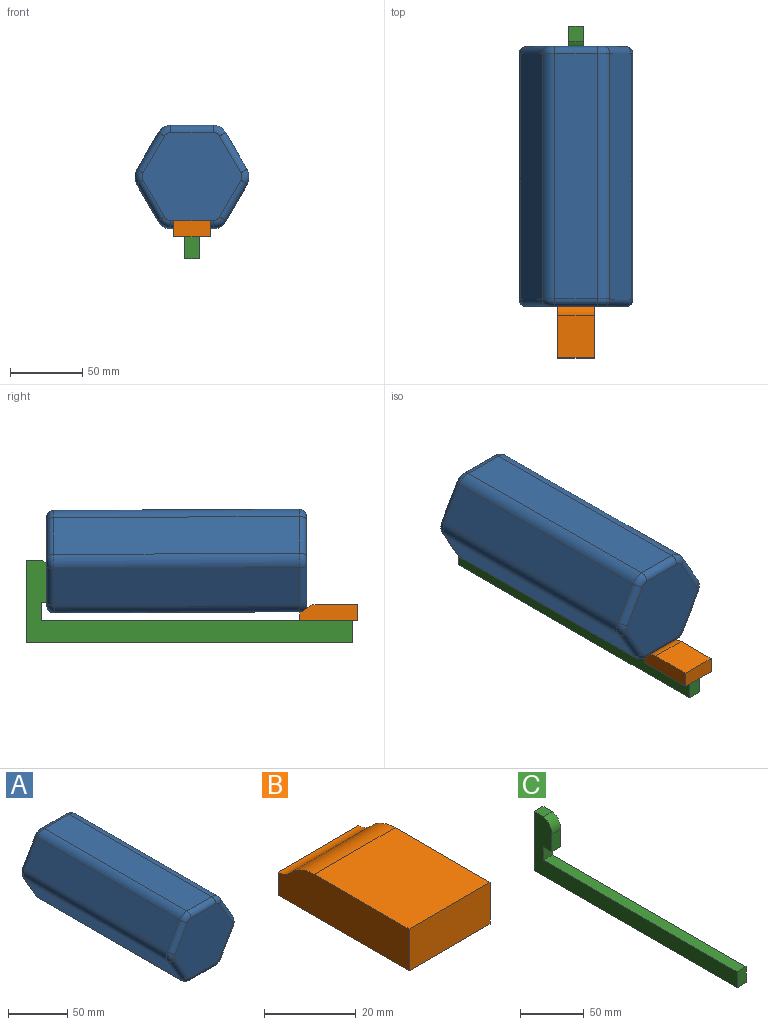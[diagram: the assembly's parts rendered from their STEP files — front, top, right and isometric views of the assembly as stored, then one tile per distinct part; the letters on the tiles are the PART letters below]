
ASSEMBLY  parts=3 mates=2
PART A: 47 faces, bbox 80.6x180x72.7 mm
  f0: plane 68.91x61.01mm, normal (0,1,0), area 2910.8mm2, adj f1,f15,f16,f17,f18,f19,f20,f21
  f1: cylinder r=5mm len=9.73mm, axis (1,0,0), area 76.4mm2, adj f0,f12,f17,f42
  f2: plane 170x25.51mm, normal (0.87,0,-0.5), area 5007mm2, adj f3,f13,f19,f31
  f3: cylinder r=10mm len=170mm, axis (0,1,0), area 1780.2mm2, adj f2,f4,f21,f33
  f4: plane 170x25.51mm, normal (0.87,0,0.5), area 5007mm2, adj f3,f5,f23,f35
  f5: cylinder r=10mm len=170mm, axis (0,1,0), area 1780.2mm2, adj f4,f6,f25,f37
  f6: plane 170x29.45mm, normal (0,0,1), area 5007mm2, adj f5,f7,f26,f38
  f7: cylinder r=10mm len=170mm, axis (0,1,0), area 1780.2mm2, adj f6,f8,f24,f36
  f8: plane 170x25.51mm, normal (-0.87,0,0.5), area 5007mm2, adj f7,f9,f22,f34
  f9: cylinder r=10mm len=170mm, axis (0,1,0), area 1780.2mm2, adj f8,f10,f20,f32
  f10: plane 170x25.51mm, normal (-0.87,0,-0.5), area 5007mm2, adj f9,f11,f18,f30
  f11: cylinder r=10mm len=170mm, axis (0,1,0), area 1780.2mm2, adj f10,f12,f16,f28
  f12: plane 170x29.45mm, normal (0,0,-1), area 5007mm2, adj f1,f11,f13,f15,f27,f44
  f13: cylinder r=10mm len=170mm, axis (0,1,0), area 1780.2mm2, adj f2,f12,f17,f29
  f14: plane 68.91x61.01mm, normal (0,-1,0), area 3215.9mm2, adj f27,f28,f29,f30,f31,f32,f33,f34
  f15: cylinder r=5mm len=9.73mm, axis (1,0,0), area 76.4mm2, adj f0,f12,f16,f43
  f16: torus R=5mm, axis (0,-1,0), area 67.3mm2, adj f0,f11,f15,f18
  f17: torus R=5mm, axis (0,-1,0), area 67.3mm2, adj f0,f1,f13,f19
  f18: cylinder r=5mm len=28.01mm, axis (0.5,0,-0.87), area 231.3mm2, adj f0,f10,f16,f20
  f19: cylinder r=5mm len=28.01mm, axis (0.5,0,0.87), area 231.3mm2, adj f0,f2,f17,f21
  f20: torus R=5mm, axis (0,-1,0), area 67.3mm2, adj f0,f9,f18,f22
  f21: torus R=5mm, axis (0,-1,0), area 67.3mm2, adj f0,f3,f19,f23
  f22: cylinder r=5mm len=28.01mm, axis (-0.5,0,-0.87), area 231.3mm2, adj f0,f8,f20,f24
  f23: cylinder r=5mm len=28.01mm, axis (-0.5,0,0.87), area 231.3mm2, adj f0,f4,f21,f25
  f24: torus R=5mm, axis (0,-1,0), area 67.3mm2, adj f0,f7,f22,f26
  f25: torus R=5mm, axis (0,-1,0), area 67.3mm2, adj f0,f5,f23,f26
  f26: cylinder r=5mm len=29.45mm, axis (-1,0,0), area 231.3mm2, adj f0,f6,f24,f25
  f27: cylinder r=5mm len=29.45mm, axis (-1,0,0), area 231.3mm2, adj f12,f14,f28,f29
  f28: torus R=5mm, axis (0,-1,0), area 67.3mm2, adj f11,f14,f27,f30
  f29: torus R=5mm, axis (0,-1,0), area 67.3mm2, adj f13,f14,f27,f31
  f30: cylinder r=5mm len=28.01mm, axis (-0.5,0,0.87), area 231.3mm2, adj f10,f14,f28,f32
  f31: cylinder r=5mm len=28.01mm, axis (-0.5,0,-0.87), area 231.3mm2, adj f2,f14,f29,f33
  f32: torus R=5mm, axis (0,-1,0), area 67.3mm2, adj f9,f14,f30,f34
  f33: torus R=5mm, axis (0,-1,0), area 67.3mm2, adj f3,f14,f31,f35
  f34: cylinder r=5mm len=28.01mm, axis (0.5,0,0.87), area 231.3mm2, adj f8,f14,f32,f36
  f35: cylinder r=5mm len=28.01mm, axis (0.5,0,-0.87), area 231.3mm2, adj f4,f14,f33,f37
  f36: torus R=5mm, axis (0,-1,0), area 67.3mm2, adj f7,f14,f34,f38
  f37: torus R=5mm, axis (0,-1,0), area 67.3mm2, adj f5,f14,f35,f38
  f38: cylinder r=5mm len=29.45mm, axis (1,0,0), area 231.3mm2, adj f6,f14,f36,f37
  f39: cylinder r=12.48mm len=12.09mm, axis (-1,0,0), area 164.6mm2, adj f0,f40,f42,f43
  f40: plane 16.95x10mm, normal (0,1,0), area 169.5mm2, adj f39,f41,f42,f43
  f41: plane 10x8.36mm, normal (0,0,1), area 83.6mm2, adj f40,f42,f43,f46
  f42: plane 35.51x9.36mm, normal (-1,0,0), area 251.1mm2, adj f0,f1,f39,f40,f41,f44,f45,f46
  f43: plane 35.51x9.36mm, normal (1,0,0), area 251.1mm2, adj f0,f15,f39,f40,f41,f44,f45,f46
  f44: plane 10x1mm, normal (0,1,0), area 10mm2, adj f12,f42,f43,f45
  f45: cylinder r=4mm len=10mm, axis (1,0,0), area 62.8mm2, adj f42,f43,f44,f46
  f46: plane 10x1.47mm, normal (0,1,0), area 14.7mm2, adj f41,f42,f43,f45
PART B: 8 faces, bbox 25x40.5x11.2 mm
  f0: plane 25x6.16mm, normal (0,1,0), area 154mm2, adj f1,f5,f6,f7
  f1: cylinder r=5mm len=25mm, axis (-1,0,0), area 105.1mm2, adj f0,f2,f6,f7
  f2: cylinder r=10mm len=25mm, axis (-1,0,0), area 210.3mm2, adj f1,f3,f6,f7
  f3: plane 29.27x25mm, normal (0,0,1), area 731.7mm2, adj f2,f4,f6,f7
  f4: plane 25x11.16mm, normal (0,-1,0), area 279mm2, adj f3,f5,f6,f7
  f5: plane 40.45x25mm, normal (0,0,-1), area 1011.3mm2, adj f0,f4,f6,f7
  f6: plane 40.45x11.16mm, normal (1,0,0), area 427mm2, adj f0,f1,f2,f3,f4,f5
  f7: plane 40.45x11.16mm, normal (-1,0,0), area 427mm2, adj f0,f1,f2,f3,f4,f5
PART C: 11 faces, bbox 10x225.9x57 mm
  f0: cylinder r=12.48mm len=12.09mm, axis (-1,0,0), area 164.6mm2, adj f1,f3,f4,f10
  f1: plane 16.95x10mm, normal (0,-1,0), area 169.5mm2, adj f0,f2,f3,f4
  f2: plane 10x9.36mm, normal (0,0,-1), area 93.6mm2, adj f1,f3,f4,f5
  f3: plane 225.88x56.95mm, normal (1,0,0), area 4130mm2, adj f0,f1,f2,f5,f6,f7,f8,f9
  f4: plane 225.88x56.95mm, normal (-1,0,0), area 4130mm2, adj f0,f1,f2,f5,f6,f7,f8,f9
  f5: plane 12.63x10mm, normal (0,-1,0), area 126.3mm2, adj f2,f3,f4,f6
  f6: plane 215.45x10mm, normal (0,0,1), area 2154.5mm2, adj f3,f4,f5,f7
  f7: plane 15.29x10mm, normal (0,-1,0), area 152.9mm2, adj f3,f4,f6,f8
  f8: plane 225.88x10mm, normal (0,0,-1), area 2258.8mm2, adj f3,f4,f7,f9
  f9: plane 56.95x10mm, normal (0,1,0), area 569.5mm2, adj f3,f4,f8,f10
  f10: plane 10.43x10mm, normal (0,0,1), area 104.3mm2, adj f0,f3,f4,f9
PLACE A rot(axis=(-1,0,0),0.3deg) t=(18.55,-229.01,-15.17)mm
PLACE B t=(18.55,-229.15,-14.33)mm
PLACE C t=(18.55,-225.18,-14.33)mm fixed
MATE slider B.f4 <-> C.f7  axis (0,-1,0) through (18.55,-444.6,-56)mm
MATE revolute B.f1 <-> A.f27  axis (1,0,0) through (31.05,-404.15,-44.84)mm
